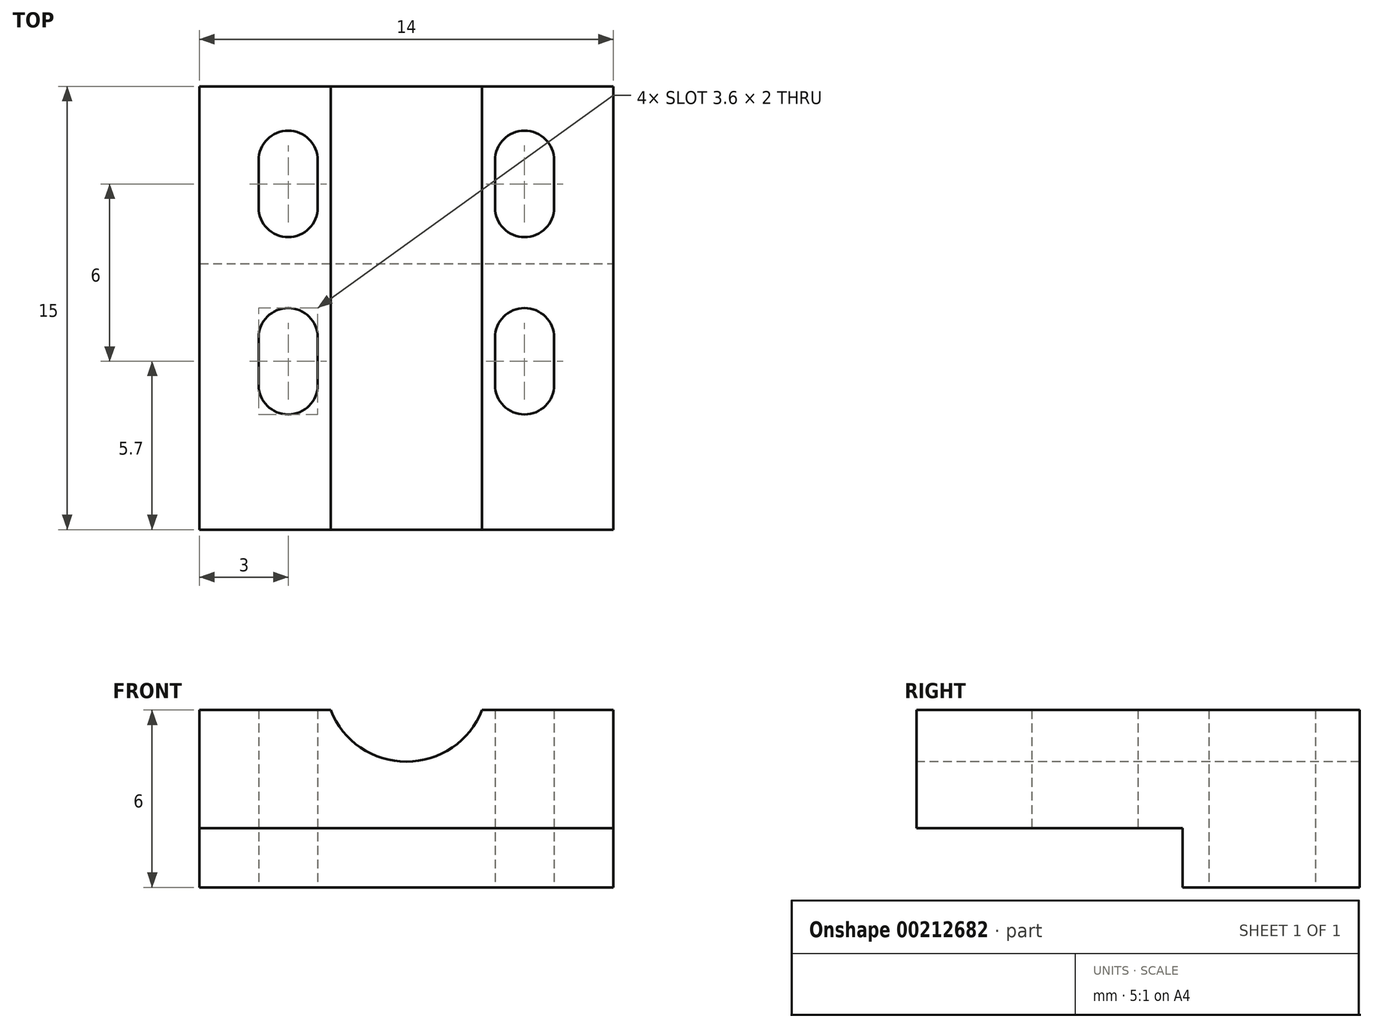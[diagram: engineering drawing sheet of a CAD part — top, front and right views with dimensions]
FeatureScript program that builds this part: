
annotation { "Feature Type Name" : "Feature", "Feature Type Description" : "" }
export const myFeature = defineFeature(function(context is Context, id is Id, definition is map)
    precondition{}
    {
        {
            var Q0;
            Q0=qCreatedBy(makeId("Top.planeOp"),FACE);
            var sketch = newSketch(context, id + "F0", { "sketchPlane" : qUnion([Q0])});
            skLineSegment(sketch, "E0.bottom", {"start": v(-7, 15) * mm, "end": v(7, 15) * mm});
            skLineSegment(sketch, "E0.top", {"start": v(-7, 0) * mm, "end": v(7, 0) * mm});
            skLineSegment(sketch, "E0.left", {"start": v(-7, 15) * mm, "end": v(-7, 0) * mm});
            skLineSegment(sketch, "E0.right", {"start": v(7, 15) * mm, "end": v(7, 0) * mm});
            skLineSegment(sketch, "E1.bottom", {"start": v(-5, 6.5) * mm, "end": v(-3, 6.5) * mm, "construction": true});
            skLineSegment(sketch, "E1.top", {"start": v(-5, 4.9) * mm, "end": v(-3, 4.9) * mm, "construction": true});
            skLineSegment(sketch, "E1.left", {"start": v(-5, 6.5) * mm, "end": v(-5, 4.9) * mm});
            skLineSegment(sketch, "E1.right", {"start": v(-3, 6.5) * mm, "end": v(-3, 4.9) * mm});
            skLineSegment(sketch, "E2.bottom", {"start": v(-5, 12.5) * mm, "end": v(-3, 12.5) * mm, "construction": true});
            skLineSegment(sketch, "E2.top", {"start": v(-5, 10.9) * mm, "end": v(-3, 10.9) * mm, "construction": true});
            skLineSegment(sketch, "E2.left", {"start": v(-5, 12.5) * mm, "end": v(-5, 10.9) * mm});
            skLineSegment(sketch, "E2.right", {"start": v(-3, 12.5) * mm, "end": v(-3, 10.9) * mm});
            skArc(sketch, "E3", {"start": v(-3, 12.5) * mm, "mid": v(-4, 13.5) * mm, "end": v(-5, 12.5) * mm});
            skArc(sketch, "E4", {"start": v(-5, 10.9) * mm, "mid": v(-4, 9.9) * mm, "end": v(-3, 10.9) * mm});
            skArc(sketch, "E5", {"start": v(-3, 6.5) * mm, "mid": v(-4, 7.5) * mm, "end": v(-5, 6.5) * mm});
            skArc(sketch, "E6", {"start": v(-5, 4.9) * mm, "mid": v(-4, 3.9) * mm, "end": v(-3, 4.9) * mm});
            skArc(sketch, "E7.MirrorCS", {"start": v(3, 12.5) * mm, "mid": v(4, 13.5) * mm, "end": v(5, 12.5) * mm});
            skArc(sketch, "E8.MirrorCS", {"start": v(5, 4.9) * mm, "mid": v(4, 3.9) * mm, "end": v(3, 4.9) * mm});
            skArc(sketch, "E9.MirrorCS", {"start": v(3, 6.5) * mm, "mid": v(4, 7.5) * mm, "end": v(5, 6.5) * mm});
            skLineSegment(sketch, "E10.MirrorCS", {"start": v(3, 12.5) * mm, "end": v(3, 10.9) * mm});
            skArc(sketch, "E11.MirrorCS", {"start": v(5, 10.9) * mm, "mid": v(4, 9.9) * mm, "end": v(3, 10.9) * mm});
            skLineSegment(sketch, "E12.MirrorCS", {"start": v(5, 12.5) * mm, "end": v(5, 10.9) * mm});
            skLineSegment(sketch, "E13.MirrorCS", {"start": v(5, 10.9) * mm, "end": v(3, 10.9) * mm, "construction": true});
            skLineSegment(sketch, "E14.MirrorCS", {"start": v(3, 6.5) * mm, "end": v(3, 4.9) * mm});
            skLineSegment(sketch, "E15.MirrorCS", {"start": v(5, 4.9) * mm, "end": v(3, 4.9) * mm, "construction": true});
            skLineSegment(sketch, "E16.MirrorCS", {"start": v(5, 6.5) * mm, "end": v(5, 4.9) * mm});
            skLineSegment(sketch, "E17.MirrorCS", {"start": v(5, 6.5) * mm, "end": v(3, 6.5) * mm, "construction": true});
            skLineSegment(sketch, "E18.MirrorCS", {"start": v(5, 12.5) * mm, "end": v(3, 12.5) * mm, "construction": true});
            skSolve(sketch);
        }
        {
            var Q0;
            Q0 = qSketchRegion(id + "F0", true);
            extrude(context, id + "F1", {"entities" : qUnion([Q0]), "depth" : 4 * mm});
        }
        {
            var Q0;
            Q0=makeQuery(id+"F1.opExtrude","SWEPT_FACE",FACE,{"disambiguationData":[OSD([sQuery(id+"F0.wireOp",EDGE,"E0.top")])]});
            var sketch = newSketch(context, id + "F2", { "sketchPlane" : qUnion([Q0])});
            skArc(sketch, "E19", {"start": v(-2.75, 5) * mm, "mid": v(0, 2.25) * mm, "end": v(2.75, 5) * mm});
            skLineSegment(sketch, "E20", {"start": v(-2.75, 4) * mm, "end": v(-2.75, 5) * mm});
            skLineSegment(sketch, "E21", {"start": v(-2.75, 4) * mm, "end": v(2.75, 4) * mm});
            skLineSegment(sketch, "E22", {"start": v(2.75, 5) * mm, "end": v(2.75, 4) * mm});
            skSolve(sketch);
        }
        {
            var Q0;
            Q0 = qSketchRegion(id + "F2", true);
            extrude(context, id + "F3", {"entities" : qUnion([Q0]), "operationType" : NewBodyOperationType.REMOVE, "endBound" : BoundingType.THROUGH_ALL, "oppositeDirection" : true, "depth" : 25 * mm});
        }
        {
            var Q0;
            Q0=makeQuery(id+"F1.opExtrude","CAP_FACE",FACE,{"disambiguationData":[OSD([sQuery(id+"F0.wireOp",EDGE,"E0.bottom"),sQuery(id+"F0.wireOp",EDGE,"E0.top"),sQuery(id+"F0.wireOp",EDGE,"E0.left"),sQuery(id+"F0.wireOp",EDGE,"E0.right"),sQuery(id+"F0.wireOp",EDGE,"E1.left"),sQuery(id+"F0.wireOp",EDGE,"E1.right"),sQuery(id+"F0.wireOp",EDGE,"E2.left"),sQuery(id+"F0.wireOp",EDGE,"E2.right"),sQuery(id+"F0.wireOp",EDGE,"E3"),sQuery(id+"F0.wireOp",EDGE,"E4"),sQuery(id+"F0.wireOp",EDGE,"E5"),sQuery(id+"F0.wireOp",EDGE,"E6"),sQuery(id+"F0.wireOp",EDGE,"E7.MirrorCS"),sQuery(id+"F0.wireOp",EDGE,"E8.MirrorCS"),sQuery(id+"F0.wireOp",EDGE,"E9.MirrorCS"),sQuery(id+"F0.wireOp",EDGE,"E10.MirrorCS"),sQuery(id+"F0.wireOp",EDGE,"E11.MirrorCS"),sQuery(id+"F0.wireOp",EDGE,"E12.MirrorCS"),sQuery(id+"F0.wireOp",EDGE,"E14.MirrorCS"),sQuery(id+"F0.wireOp",EDGE,"E16.MirrorCS")])],"isStart":true});
            var sketch = newSketch(context, id + "F4", { "sketchPlane" : qUnion([Q0])});
            skLineSegment(sketch, "E23.bottom", {"start": v(-7, -15) * mm, "end": v(7, -15) * mm});
            skLineSegment(sketch, "E23.top", {"start": v(-7, -9) * mm, "end": v(7, -9) * mm});
            skLineSegment(sketch, "E23.left", {"start": v(-7, -15) * mm, "end": v(-7, -9) * mm});
            skLineSegment(sketch, "E23.right", {"start": v(7, -15) * mm, "end": v(7, -9) * mm});
            skSolve(sketch);
        }
        {
            var Q0;
            Q0=makeQuery(id+"F4.imprint","IMPRINT",FACE,{"disambiguationData":[TD([[makeQuery(id+"F4.imprint","IMPRINT",EDGE,{"derivedFrom":sQuery(id+"F4.wireOp",EDGE,"E23.bottom")}),1.0]])]});
            extrude(context, id + "F5", {"entities" : qUnion([Q0]), "operationType" : NewBodyOperationType.ADD, "depth" : 2 * mm});
        }
    });
